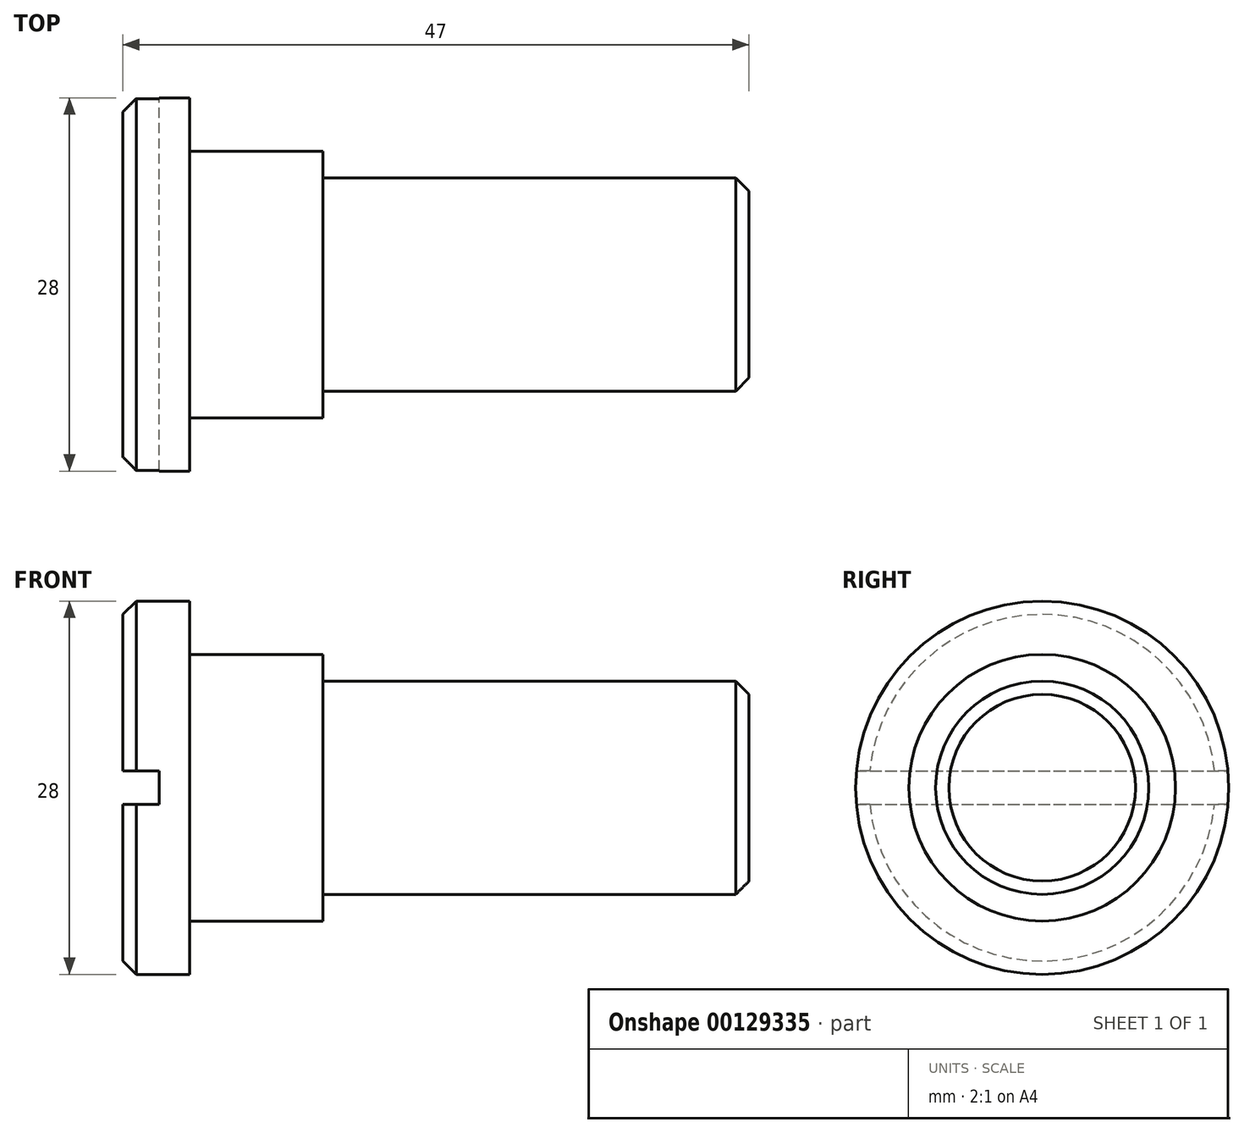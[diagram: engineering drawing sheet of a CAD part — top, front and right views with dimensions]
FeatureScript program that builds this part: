
annotation { "Feature Type Name" : "Feature", "Feature Type Description" : "" }
export const myFeature = defineFeature(function(context is Context, id is Id, definition is map)
    precondition{}
    {
        {
            var Q0;
            Q0=qCreatedBy(makeId("Right.planeOp"),FACE);
            var sketch = newSketch(context, id + "F0", { "sketchPlane" : qUnion([Q0])});
            skCircle(sketch, "E0", {"center": v(0, 0) * mm, "radius": 10 * mm});
            skCircle(sketch, "E1", {"center": v(0, 0) * mm, "radius": 14 * mm});
            skCircle(sketch, "E2", {"center": v(0, 0) * mm, "radius": 8 * mm});
            skSolve(sketch);
        }
        {
            var Q0;
            Q0=makeQuery(id+"F0.imprint","IMPRINT",FACE,{"disambiguationData":[TD([[makeQuery(id+"F0.imprint","IMPRINT",EDGE,{"derivedFrom":sQuery(id+"F0.wireOp",EDGE,"E2")}),1.0]])]});
            extrude(context, id + "F1", {"entities" : qUnion([Q0]), "depth" : 42 * mm, "hasSecondDirection" : true, "secondDirectionOppositeDirection" : true, "secondDirectionDepth" : 5 * mm});
        }
        {
            var Q0;
            Q0=makeQuery(id+"F0.imprint","IMPRINT",FACE,{"disambiguationData":[TD([[makeQuery(id+"F0.imprint","IMPRINT",EDGE,{"derivedFrom":sQuery(id+"F0.wireOp",EDGE,"E0")}),1.0]])]});
            extrude(context, id + "F2", {"entities" : qUnion([Q0]), "operationType" : NewBodyOperationType.ADD, "depth" : 10 * mm, "hasSecondDirection" : true, "secondDirectionOppositeDirection" : true, "secondDirectionDepth" : 5 * mm});
        }
        {
            var Q0;
            Q0=makeQuery(id+"F0.imprint","IMPRINT",FACE,{"disambiguationData":[TD([[makeQuery(id+"F0.imprint","IMPRINT",EDGE,{"derivedFrom":sQuery(id+"F0.wireOp",EDGE,"E0")}),-1.0]])]});
            extrude(context, id + "F3", {"entities" : qUnion([Q0]), "operationType" : NewBodyOperationType.ADD, "oppositeDirection" : true, "depth" : 5 * mm});
        }
        {
            var Q0;
            Q0=makeQuery(id+"F3.opExtrude","CAP_EDGE",EDGE,{"disambiguationData":[OSD([sQuery(id+"F0.wireOp",EDGE,"E1")])],"isStart":false});
            var Q1;
            Q1=makeQuery(id+"F1.opExtrude","CAP_EDGE",EDGE,{"disambiguationData":[OSD([sQuery(id+"F0.wireOp",EDGE,"E2")])],"isStart":false});
            chamfer(context, id + "F4", {"entities" : qUnion([Q0, Q1]), "width" : 1 * mm, "tangentPropagation" : true});
        }
        {
            var Q0;
            Q0=qCreatedBy(makeId("Front.planeOp"),FACE);
            var sketch = newSketch(context, id + "F5", { "sketchPlane" : qUnion([Q0])});
            skLineSegment(sketch, "E3.bottom", {"start": v(-2.28, -1.25) * mm, "end": v(-60.28, -1.25) * mm});
            skLineSegment(sketch, "E3.top", {"start": v(-2.28, 1.25) * mm, "end": v(-60.28, 1.25) * mm});
            skLineSegment(sketch, "E3.left", {"start": v(-2.28, -1.25) * mm, "end": v(-2.28, 1.25) * mm});
            skLineSegment(sketch, "E3.right", {"start": v(-60.28, -1.25) * mm, "end": v(-60.28, 1.25) * mm});
            skPoint(sketch, "E3.middle", {"position": v(-31.28, 0) * mm});
            skSolve(sketch);
        }
        {
            var Q0;
            Q0=makeQuery(id+"F5.imprint","IMPRINT",FACE,{"disambiguationData":[TD([[makeQuery(id+"F5.imprint","IMPRINT",EDGE,{"derivedFrom":sQuery(id+"F5.wireOp",EDGE,"E3.bottom")}),-1.0]])]});
            extrude(context, id + "F6", {"entities" : qUnion([Q0]), "operationType" : NewBodyOperationType.REMOVE, "depth" : 25 * mm, "hasSecondDirection" : true, "secondDirectionOppositeDirection" : true, "secondDirectionDepth" : 25 * mm});
        }
    });
